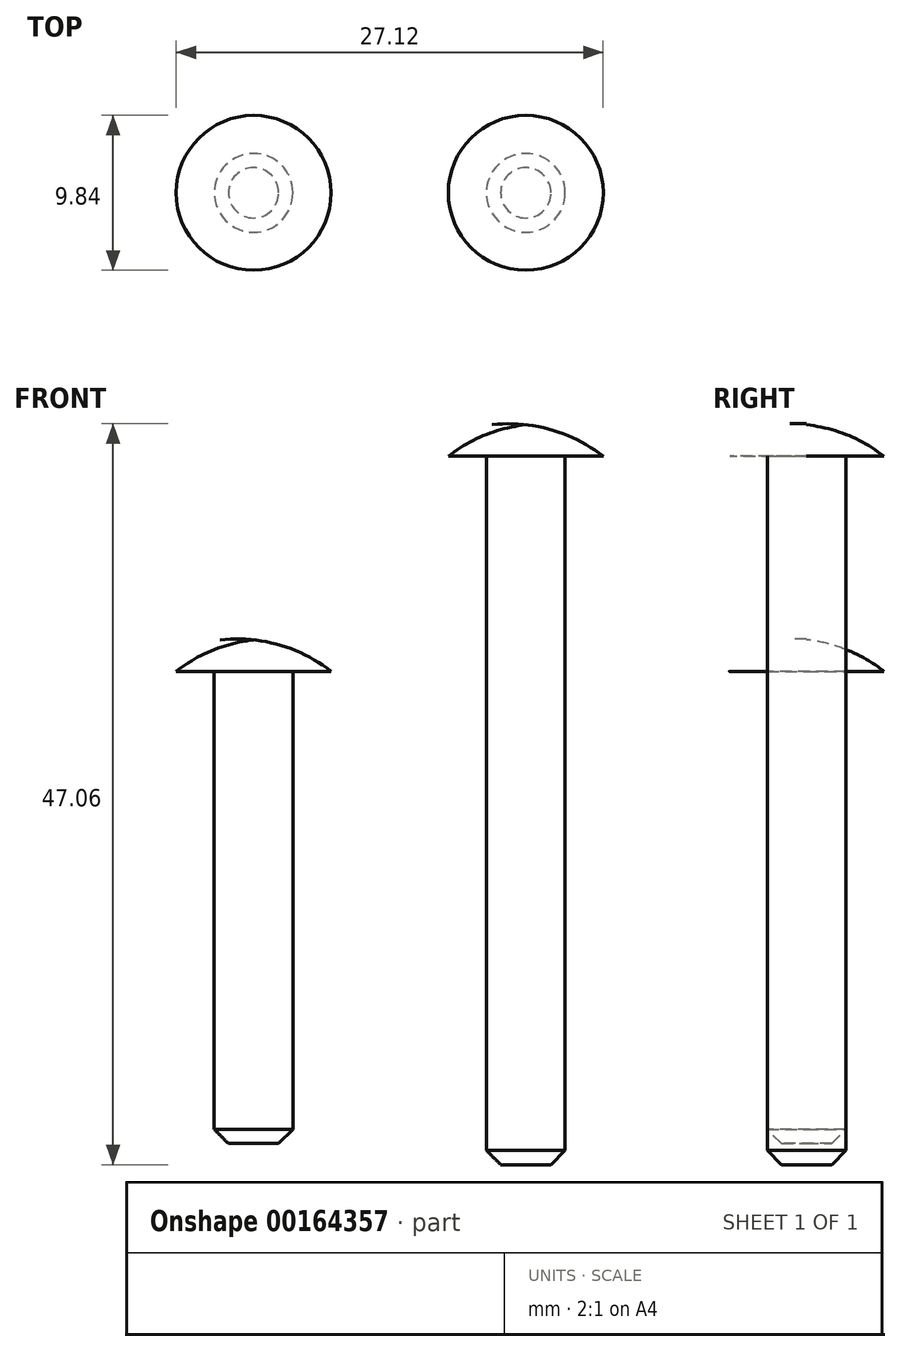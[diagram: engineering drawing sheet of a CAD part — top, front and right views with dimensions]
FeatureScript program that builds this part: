
annotation { "Feature Type Name" : "Feature", "Feature Type Description" : "" }
export const myFeature = defineFeature(function(context is Context, id is Id, definition is map)
    precondition{}
    {
        {
            var Q0;
            Q0=qCreatedBy(makeId("Front.planeOp"),FACE);
            var sketch = newSketch(context, id + "F0", { "sketchPlane" : qUnion([Q0])});
            skLineSegment(sketch, "E0", {"start": v(0, -8.06) * mm, "end": v(1.6, -8.06) * mm});
            skLineSegment(sketch, "E1", {"start": v(1.6, -8.06) * mm, "end": v(2.5, -7.16) * mm});
            skLineSegment(sketch, "E2", {"start": v(2.5, -7.16) * mm, "end": v(2.5, 21.94) * mm});
            skLineSegment(sketch, "E3", {"start": v(0, 21.94) * mm, "end": v(4.92, 21.94) * mm});
            skArc(sketch, "E4", {"start": v(4.92, 21.94) * mm, "mid": v(2.6, 23.28) * mm, "end": v(0, 23.94) * mm});
            skLineSegment(sketch, "E5", {"start": v(0, -8.06) * mm, "end": v(0, 21.94) * mm});
            skLineSegment(sketch, "E6", {"start": v(0, 21.94) * mm, "end": v(0, 23.94) * mm});
            skSolve(sketch);
        }
        {
            var Q0;
            Q0=qSketchRegion(id+"F0",true);
            var Q1;
            Q1=sQuery(id+"F0.wireOp",EDGE,"E5");
            revolve(context, id + "F1", {"entities" : qUnion([Q0]), "axis" : qUnion([Q1]), "revolveType" : RevolveType.FULL});
        }
        {
            var Q0;
            Q0=qCreatedBy(makeId("Front.planeOp"),FACE);
            var sketch = newSketch(context, id + "F2", { "sketchPlane" : qUnion([Q0])});
            skLineSegment(sketch, "E7", {"start": v(17.29, -9.4) * mm, "end": v(18.88, -9.4) * mm});
            skLineSegment(sketch, "E8", {"start": v(18.88, -9.4) * mm, "end": v(19.79, -8.5) * mm});
            skLineSegment(sketch, "E9", {"start": v(19.79, -8.5) * mm, "end": v(19.79, 35.6) * mm});
            skLineSegment(sketch, "E10", {"start": v(17.29, 35.6) * mm, "end": v(22.2, 35.6) * mm});
            skArc(sketch, "E11", {"start": v(22.2, 35.6) * mm, "mid": v(19.88, 36.94) * mm, "end": v(17.29, 37.6) * mm});
            skLineSegment(sketch, "E12", {"start": v(17.29, -9.4) * mm, "end": v(17.29, 35.6) * mm});
            skLineSegment(sketch, "E13", {"start": v(17.29, 35.6) * mm, "end": v(17.29, 37.6) * mm});
            skSolve(sketch);
        }
        {
            var Q0;
            Q0 = qSketchRegion(id + "F2", true);
            var Q1;
            Q1=sQuery(id+"F2.wireOp",EDGE,"E12");
            revolve(context, id + "F3", {"entities" : qUnion([Q0]), "axis" : qUnion([Q1]), "revolveType" : RevolveType.FULL});
        }
    });
